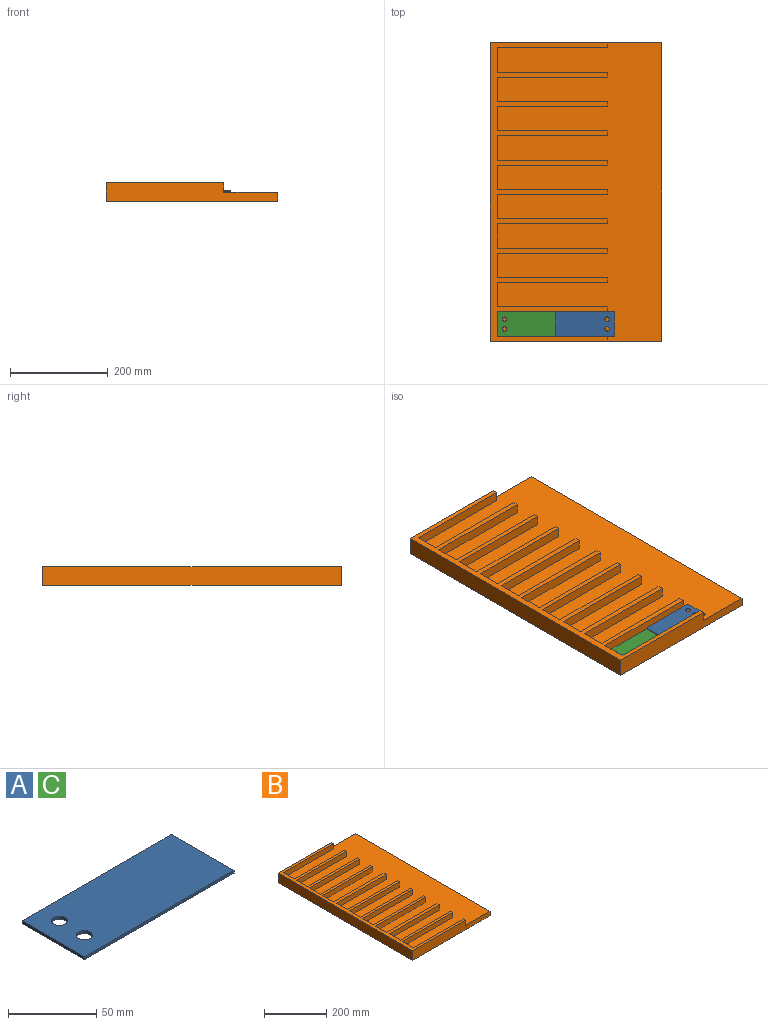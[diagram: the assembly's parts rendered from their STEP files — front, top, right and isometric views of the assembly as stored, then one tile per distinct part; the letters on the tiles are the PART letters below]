
ASSEMBLY  parts=3 mates=2
PART A: 8 faces, bbox 120x50x2 mm
  f0: plane 120x2mm, normal (0,1,0), area 240mm2, adj f1,f3,f4,f5
  f1: plane 50x2mm, normal (-1,0,0), area 100mm2, adj f0,f2,f4,f5
  f2: plane 120x2mm, normal (0,-1,0), area 240mm2, adj f1,f3,f4,f5
  f3: plane 50x2mm, normal (1,0,0), area 100mm2, adj f0,f2,f4,f5
  f4: plane 120x50mm, normal (0,0,1), area 5872.8mm2, adj f0,f1,f2,f3,f6,f7
  f5: plane 120x50mm, normal (0,0,-1), area 5872.8mm2, adj f0,f1,f2,f3,f6,f7
  f6: cylinder r=4.5mm len=9mm, axis (0,0,1), area 56.5mm2, adj f4,f5
  f7: cylinder r=4.5mm len=9mm, axis (0,0,1), area 56.5mm2, adj f4,f5
PART B: 48 faces, bbox 350x610x38 mm
  f0: plane 226.5x20mm, normal (0,1,0), area 4530mm2, adj f20,f26,f27,f47
  f1: plane 226.5x20mm, normal (0,1,0), area 4530mm2, adj f20,f27,f28,f46
  f2: plane 226.5x20mm, normal (0,-1,0), area 4530mm2, adj f20,f27,f28,f47
  f3: plane 226.5x20mm, normal (0,1,0), area 4530mm2, adj f20,f27,f29,f45
  f4: plane 226.5x20mm, normal (0,-1,0), area 4530mm2, adj f20,f27,f29,f46
  f5: plane 226.5x20mm, normal (0,1,0), area 4530mm2, adj f20,f27,f30,f44
  f6: plane 226.5x20mm, normal (0,-1,0), area 4530mm2, adj f20,f27,f30,f45
  f7: plane 226.5x20mm, normal (0,1,0), area 4530mm2, adj f20,f27,f31,f43
  f8: plane 226.5x20mm, normal (0,-1,0), area 4530mm2, adj f20,f27,f31,f44
  f9: plane 226.5x20mm, normal (0,1,0), area 4530mm2, adj f20,f27,f32,f42
  f10: plane 226.5x20mm, normal (0,-1,0), area 4530mm2, adj f20,f27,f32,f43
  f11: plane 226.5x20mm, normal (0,1,0), area 4530mm2, adj f20,f27,f33,f41
  f12: plane 226.5x20mm, normal (0,-1,0), area 4530mm2, adj f20,f27,f33,f42
  f13: plane 226.5x20mm, normal (0,1,0), area 4530mm2, adj f20,f27,f34,f40
  f14: plane 226.5x20mm, normal (0,-1,0), area 4530mm2, adj f20,f27,f34,f41
  f15: plane 226.5x20mm, normal (0,1,0), area 4530mm2, adj f20,f27,f35,f39
  f16: plane 226.5x20mm, normal (0,-1,0), area 4530mm2, adj f20,f27,f35,f40
  f17: plane 226.5x20mm, normal (0,1,0), area 4530mm2, adj f20,f27,f36,f38
  f18: plane 226.5x20mm, normal (0,-1,0), area 4530mm2, adj f20,f27,f36,f39
  f19: plane 226.5x20mm, normal (0,-1,0), area 4530mm2, adj f20,f27,f37,f38
  f20: plane 610x336.5mm, normal (0,0,1), area 180350mm2, adj f0,f1,f2,f3,f4,f5,f6,f7
  f21: plane 610x38mm, normal (-1,0,0), area 23180mm2, adj f22,f24,f25,f27
  f22: plane 350x38mm, normal (0,-1,0), area 11100mm2, adj f20,f21,f23,f25,f26,f27
  f23: plane 610x18mm, normal (1,0,0), area 10980mm2, adj f20,f22,f24,f25
  f24: plane 350x38mm, normal (0,1,0), area 11100mm2, adj f20,f21,f23,f25,f27,f37
  f25: plane 610x350mm, normal (0,0,-1), area 213500mm2, adj f21,f22,f23,f24
  f26: plane 20x10mm, normal (1,0,0), area 200mm2, adj f0,f20,f22,f27
  f27: plane 610x240mm, normal (0,0,1), area 33150mm2, adj f0,f1,f2,f3,f4,f5,f6,f7
  f28: plane 20x10mm, normal (1,0,0), area 200mm2, adj f1,f2,f20,f27
  f29: plane 20x10mm, normal (1,0,0), area 200mm2, adj f3,f4,f20,f27
  f30: plane 20x10mm, normal (1,0,0), area 200mm2, adj f5,f6,f20,f27
  f31: plane 20x10mm, normal (1,0,0), area 200mm2, adj f7,f8,f20,f27
  f32: plane 20x10mm, normal (1,0,0), area 200mm2, adj f9,f10,f20,f27
  f33: plane 20x10mm, normal (1,0,0), area 200mm2, adj f11,f12,f20,f27
  f34: plane 20x10mm, normal (1,0,0), area 200mm2, adj f13,f14,f20,f27
  f35: plane 20x10mm, normal (1,0,0), area 200mm2, adj f15,f16,f20,f27
  f36: plane 20x10mm, normal (1,0,0), area 200mm2, adj f17,f18,f20,f27
  f37: plane 20x10mm, normal (1,0,0), area 200mm2, adj f19,f20,f24,f27
  f38: plane 50x20mm, normal (1,0,0), area 1000mm2, adj f17,f19,f20,f27
  f39: plane 50x20mm, normal (1,0,0), area 1000mm2, adj f15,f18,f20,f27
  f40: plane 50x20mm, normal (1,0,0), area 1000mm2, adj f13,f16,f20,f27
  f41: plane 50x20mm, normal (1,0,0), area 1000mm2, adj f11,f14,f20,f27
  f42: plane 50x20mm, normal (1,0,0), area 1000mm2, adj f9,f12,f20,f27
  f43: plane 50x20mm, normal (1,0,0), area 1000mm2, adj f7,f10,f20,f27
  f44: plane 50x20mm, normal (1,0,0), area 1000mm2, adj f5,f8,f20,f27
  f45: plane 50x20mm, normal (1,0,0), area 1000mm2, adj f3,f6,f20,f27
  f46: plane 50x20mm, normal (1,0,0), area 1000mm2, adj f1,f4,f20,f27
  f47: plane 50x20mm, normal (1,0,0), area 1000mm2, adj f0,f2,f20,f27
PART C: same geometry as A
PLACE A rot(axis=(0,1,0),180deg) t=(36.69,94.16,72.42)mm
PLACE B t=(0.96,34.16,50.42)mm
PLACE C rot(axis=(1,0,0),180deg) t=(232.23,44.16,70.42)mm
MATE ball C.f4 <-> B.f20  axis (0,0,-1) through (14.46,44.16,68.42)mm
MATE planar A.f4 <-> C.f5  axis (0,0,-1) through (134.46,69.16,70.42)mm
